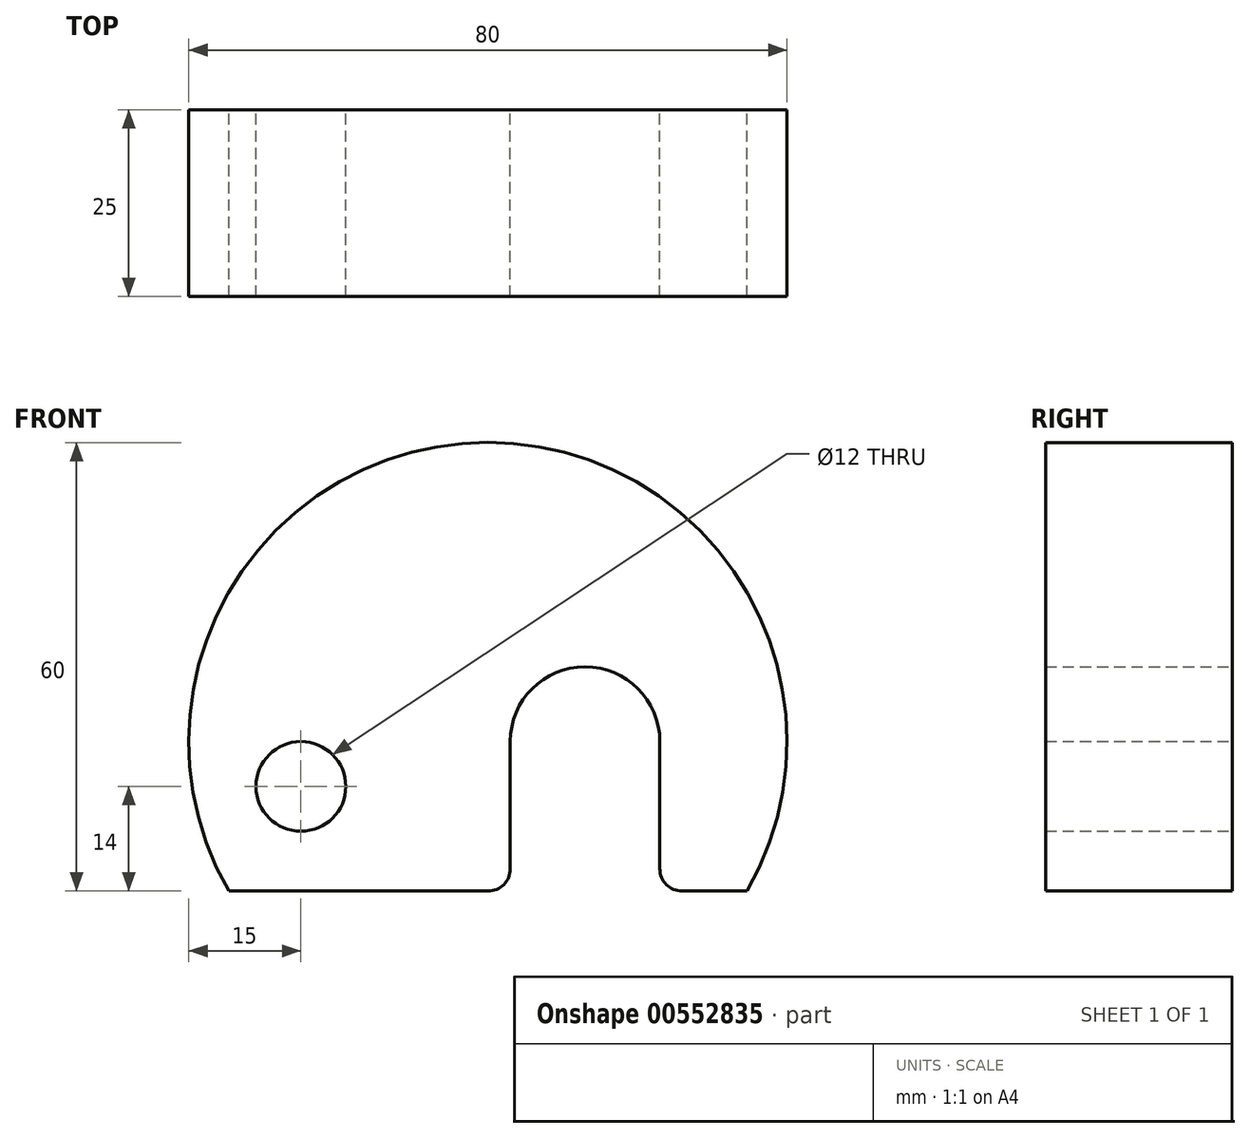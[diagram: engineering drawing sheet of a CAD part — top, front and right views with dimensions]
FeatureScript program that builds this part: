
annotation { "Feature Type Name" : "Feature", "Feature Type Description" : "" }
export const myFeature = defineFeature(function(context is Context, id is Id, definition is map)
    precondition{}
    {
        {
            var Q0;
            Q0=qCreatedBy(makeId("Front.planeOp"),FACE);
            var sketch = newSketch(context, id + "F0", { "sketchPlane" : qUnion([Q0])});
            skLineSegment(sketch, "E0", {"start": v(0, 45) * mm, "end": v(0, -50.08) * mm, "construction": true});
            skLineSegment(sketch, "E1", {"start": v(-53.96, 0) * mm, "end": v(59.02, 0) * mm, "construction": true});
            skArc(sketch, "E2", {"start": v(34.64, -20) * mm, "mid": v(0, 40) * mm, "end": v(-34.64, -20) * mm});
            skLineSegment(sketch, "E3", {"start": v(0, 5) * mm, "end": v(63.25, 5) * mm, "construction": true});
            skLineSegment(sketch, "E4", {"start": v(13, 25.45) * mm, "end": v(13, -49.03) * mm, "construction": true});
            skLineSegment(sketch, "E5", {"start": v(-25, 12.58) * mm, "end": v(-25, -41.85) * mm, "construction": true});
            skLineSegment(sketch, "E6", {"start": v(-56.92, -6) * mm, "end": v(24.5, -6) * mm, "construction": true});
            skCircle(sketch, "E7", {"center": v(-25, -6) * mm, "radius": 6 * mm});
            skArc(sketch, "E8", {"start": v(23, 0) * mm, "mid": v(13, 10) * mm, "end": v(3, 0) * mm});
            skLineSegment(sketch, "E9", {"start": v(23, 0) * mm, "end": v(23, -17) * mm});
            skLineSegment(sketch, "E10", {"start": v(3, 0) * mm, "end": v(3, -17) * mm});
            skLineSegment(sketch, "E11", {"start": v(34.64, -20) * mm, "end": v(26, -20) * mm});
            skPoint(sketch, "E12.newPointA", {"position": v(23, -20) * mm});
            skArc(sketch, "E12.filletArc", {"start": v(23, -17) * mm, "mid": v(23.88, -19.12) * mm, "end": v(26, -20) * mm});
            skLineSegment(sketch, "E13", {"start": v(0, -20) * mm, "end": v(-23.45, -20) * mm});
            skPoint(sketch, "E14.visualSharp", {"position": v(3, -20) * mm});
            skArc(sketch, "E14.filletArc", {"start": v(0, -20) * mm, "mid": v(2.12, -19.12) * mm, "end": v(3, -17) * mm});
            skLineSegment(sketch, "E15", {"start": v(-23.45, -20) * mm, "end": v(-34.64, -20) * mm});
            skSolve(sketch);
        }
        {
            var Q0;
            Q0=makeQuery(id+"F0.imprint","IMPRINT",FACE,{"disambiguationData":[TD([[makeQuery(id+"F0.imprint","IMPRINT",EDGE,{"derivedFrom":sQuery(id+"F0.wireOp",EDGE,"E2")}),1.0]])]});
            extrude(context, id + "F1", {"entities" : qUnion([Q0]), "depth" : 25 * mm, "offsetDistance" : 25 * mm});
        }
    });
